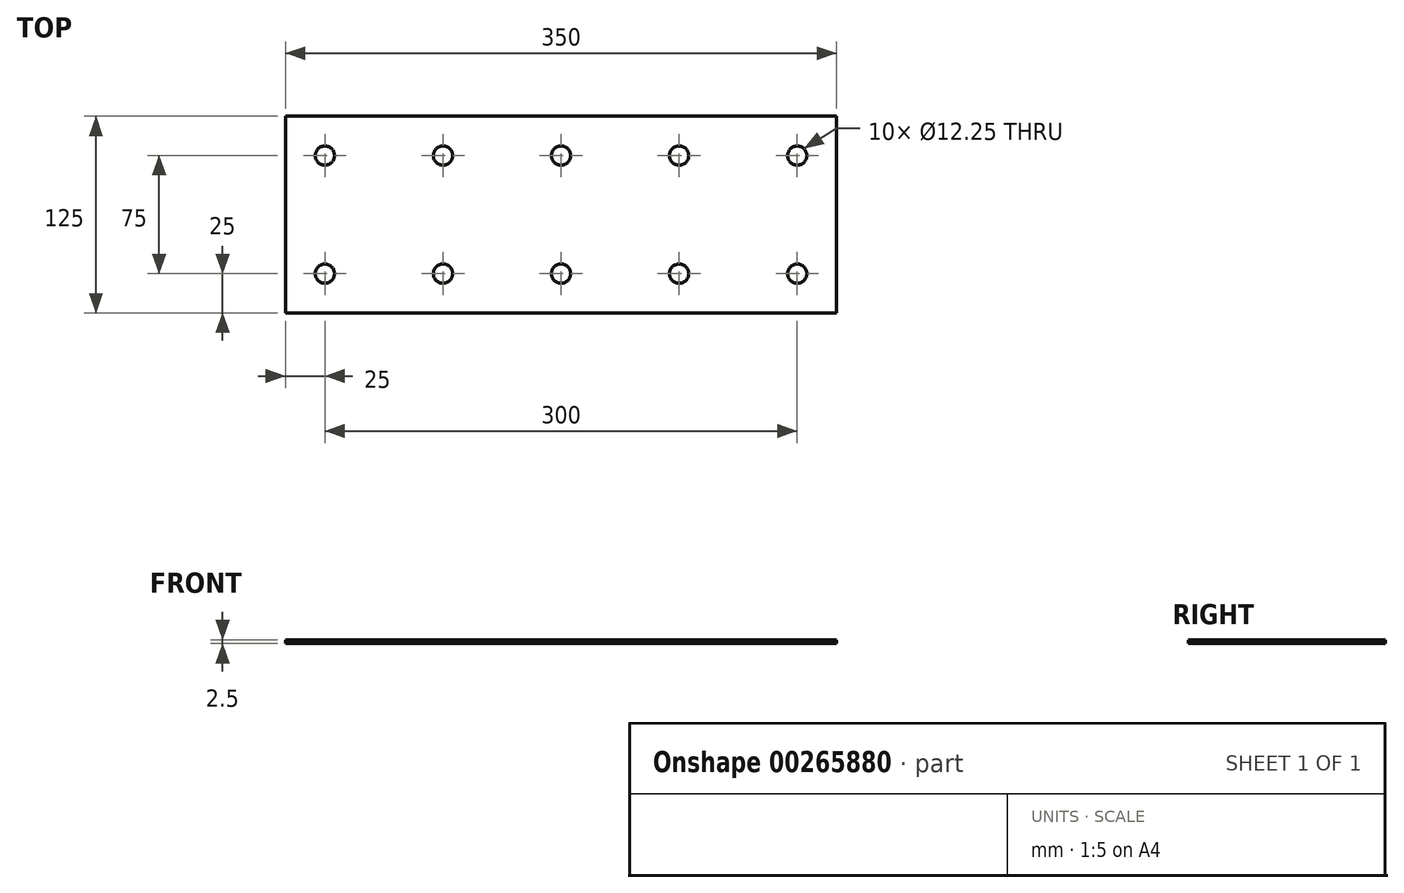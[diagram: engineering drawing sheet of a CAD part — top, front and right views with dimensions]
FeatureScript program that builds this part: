
annotation { "Feature Type Name" : "Feature", "Feature Type Description" : "" }
export const myFeature = defineFeature(function(context is Context, id is Id, definition is map)
    precondition{}
    {
        {
            var Q0;
            Q0=qCreatedBy(makeId("Top.planeOp"),FACE);
            var sketch = newSketch(context, id + "F0", { "sketchPlane" : qUnion([Q0])});
            skLineSegment(sketch, "E0.bottom", {"start": v(175, 62.5) * mm, "end": v(-175, 62.5) * mm});
            skLineSegment(sketch, "E0.top", {"start": v(175, -62.5) * mm, "end": v(-175, -62.5) * mm});
            skLineSegment(sketch, "E0.left", {"start": v(175, 62.5) * mm, "end": v(175, -62.5) * mm});
            skLineSegment(sketch, "E0.right", {"start": v(-175, 62.5) * mm, "end": v(-175, -62.5) * mm});
            skPoint(sketch, "E0.middle", {"position": v(0, 0) * mm});
            skSolve(sketch);
        }
        {
            var Q0;
            Q0=makeQuery(id+"F0.imprint","IMPRINT",FACE,{"disambiguationData":[TD([[makeQuery(id+"F0.imprint","IMPRINT",EDGE,{"derivedFrom":sQuery(id+"F0.wireOp",EDGE,"E0.bottom")}),1.0]])]});
            var sketch = newSketch(context, id + "F1", { "sketchPlane" : qUnion([Q0])});
            skCircle(sketch, "E1", {"center": v(-150, 37.5) * mm, "radius": 6.12 * mm});
            skCircle(sketch, "E2.0.1.0", {"center": v(-150, -37.5) * mm, "radius": 6.12 * mm});
            skCircle(sketch, "E2.1.0.0", {"center": v(-75, 37.5) * mm, "radius": 6.12 * mm});
            skCircle(sketch, "E2.1.1.0", {"center": v(-75, -37.5) * mm, "radius": 6.12 * mm});
            skCircle(sketch, "E2.2.0.0", {"center": v(0, 37.5) * mm, "radius": 6.12 * mm});
            skCircle(sketch, "E2.2.1.0", {"center": v(0, -37.5) * mm, "radius": 6.12 * mm});
            skCircle(sketch, "E2.3.0.0", {"center": v(75, 37.5) * mm, "radius": 6.12 * mm});
            skCircle(sketch, "E2.3.1.0", {"center": v(75, -37.5) * mm, "radius": 6.12 * mm});
            skCircle(sketch, "E2.4.0.0", {"center": v(150, 37.5) * mm, "radius": 6.12 * mm});
            skCircle(sketch, "E2.4.1.0", {"center": v(150, -37.5) * mm, "radius": 6.12 * mm});
            skLineSegment(sketch, "E2.direction1", {"start": v(-150, 37.5) * mm, "end": v(-75, 37.5) * mm, "construction": true});
            skLineSegment(sketch, "E2.direction2", {"start": v(-150, 37.5) * mm, "end": v(-150, -37.5) * mm, "construction": true});
            skSolve(sketch);
        }
        {
            var Q0;
            Q0=makeQuery(id+"F1.imprint","IMPRINT",FACE,{"disambiguationData":[TD([[makeQuery(id+"F1.imprint","IMPRINT",EDGE,{"derivedFrom":sQuery(id+"F1.wireOp",EDGE,"E1")}),-1.0]])]});
            extrude(context, id + "F2", {"entities" : qUnion([Q0]), "depth" : 2.5 * mm, "offsetDistance" : 25 * mm});
        }
    });
